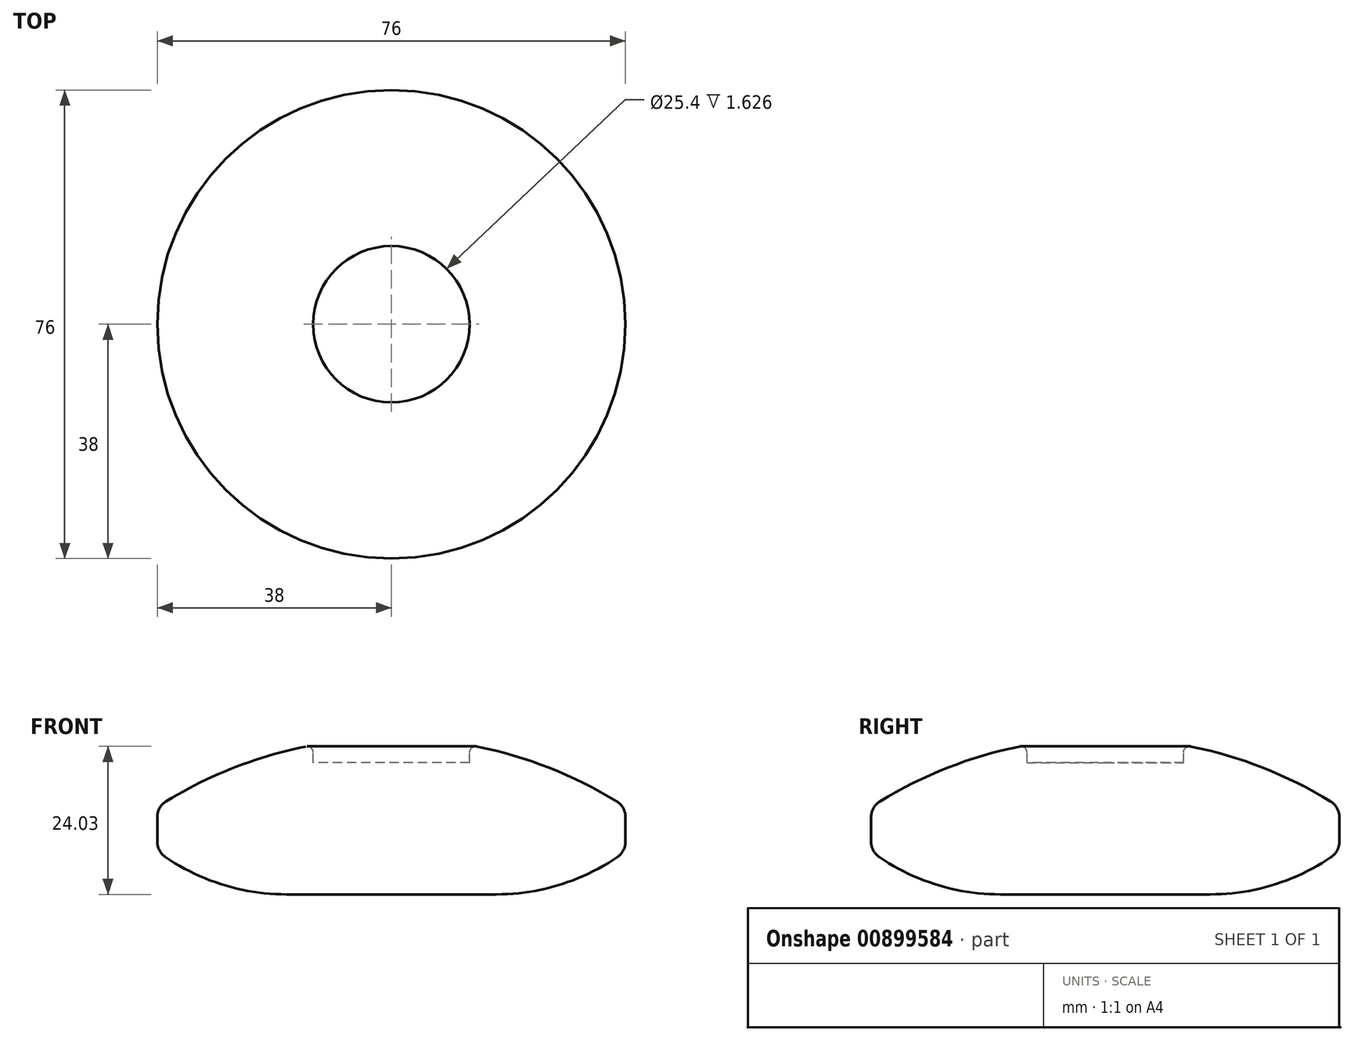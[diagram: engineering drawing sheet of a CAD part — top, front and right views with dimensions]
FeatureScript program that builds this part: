
annotation { "Feature Type Name" : "Feature", "Feature Type Description" : "" }
export const myFeature = defineFeature(function(context is Context, id is Id, definition is map)
    precondition{}
    {
        {
            var Q0;
            Q0=qCreatedBy(makeId("Front.planeOp"),FACE);
            var sketch = newSketch(context, id + "F0", { "sketchPlane" : qUnion([Q0])});
            skLineSegment(sketch, "E0", {"start": v(0, 0) * mm, "end": v(17, 0) * mm});
            skArc(sketch, "E1", {"start": v(17, 0) * mm, "mid": v(28.07, 1.8) * mm, "end": v(38, 7) * mm});
            skLineSegment(sketch, "E2", {"start": v(38, 7) * mm, "end": v(38, 14.19) * mm});
            skLineSegment(sketch, "E3", {"start": v(0, 25.4) * mm, "end": v(0, 0) * mm});
            skArc(sketch, "E4", {"start": v(38, 14.19) * mm, "mid": v(19.8, 22.54) * mm, "end": v(0, 25.4) * mm});
            skLineSegment(sketch, "E5", {"start": v(0, 25.4) * mm, "end": v(-48.53, 25.4) * mm, "construction": true});
            skSolve(sketch);
        }
        {
            var Q0;
            Q0=makeQuery(id+"F0.imprint","IMPRINT",FACE,{"disambiguationData":[TD([[makeQuery(id+"F0.imprint","IMPRINT",EDGE,{"derivedFrom":sQuery(id+"F0.wireOp",EDGE,"E0")}),1.0]])]});
            var Q1;
            Q1=sQuery(id+"F0.wireOp",EDGE,"E3");
            revolve(context, id + "F1", {"surfaceOperationType" : NewSurfaceOperationType.NEW, "entities" : qUnion([Q0]), "axis" : qUnion([Q1]), "revolveType" : RevolveType.FULL});
        }
        {
            var Q0;
            Q0=makeQuery(id+"F1.opRevolve","SWEPT_EDGE",EDGE,{"disambiguationData":[OSD([sQuery(id+"F0.wireOp",EDGE,"E1"),sQuery(id+"F0.wireOp",EDGE,"E2")])]});
            var Q1;
            Q1=makeQuery(id+"F1.opRevolve","SWEPT_EDGE",EDGE,{"disambiguationData":[OSD([sQuery(id+"F0.wireOp",EDGE,"E2"),sQuery(id+"F0.wireOp",EDGE,"E4")])]});
            fillet(context, id + "F2", {"entities" : qUnion([Q0, Q1]), "radius" : 3 * mm, "tangentPropagation" : true, "allowEdgeOverflow" : false});
        }
        {
            var Q0;
            Q0=qCreatedBy(makeId("Top.planeOp"),FACE);
            cPlane(context, id + "F3", {"entities" : qUnion([Q0]), "cplaneType" : CPlaneType.OFFSET, "offset" : 25.4 * mm, "width" : 150 * mm, "height" : 150 * mm});
        }
        {
            var Q0;
            Q0=qCreatedBy(id+"F3.planeOp",FACE);
            var sketch = newSketch(context, id + "F4", { "sketchPlane" : qUnion([Q0])});
            skCircle(sketch, "E6", {"center": v(0, 0) * mm, "radius": 12.7 * mm});
            skSolve(sketch);
        }
        {
            var Q0;
            Q0=makeQuery(id+"F4.imprint","IMPRINT",FACE,{"disambiguationData":[TD([[makeQuery(id+"F4.imprint","IMPRINT",EDGE,{"derivedFrom":sQuery(id+"F4.wireOp",EDGE,"E6")}),1.0]])]});
            extrude(context, id + "F5", {"entities" : qUnion([Q0]), "operationType" : NewBodyOperationType.REMOVE, "oppositeDirection" : true, "depth" : 4 * mm, "offsetDistance" : 25 * mm});
        }
        {
            var Q0;
            Q0=makeQuery(id+"F5.boolean.opBoolean","INTERSECT",EDGE,{"derivedFrom":[makeQuery(id+"F1.opRevolve","SWEPT_FACE",FACE,{"disambiguationData":[OSD([sQuery(id+"F0.wireOp",EDGE,"E4")])]}),makeQuery(id+"F5.opExtrude","SWEPT_FACE",FACE,{"disambiguationData":[OSD([sQuery(id+"F4.wireOp",EDGE,"E6")])]})]});
            fillet(context, id + "F6", {"entities" : qUnion([Q0]), "radius" : 1 * mm, "tangentPropagation" : true, "allowEdgeOverflow" : false});
        }
    });
